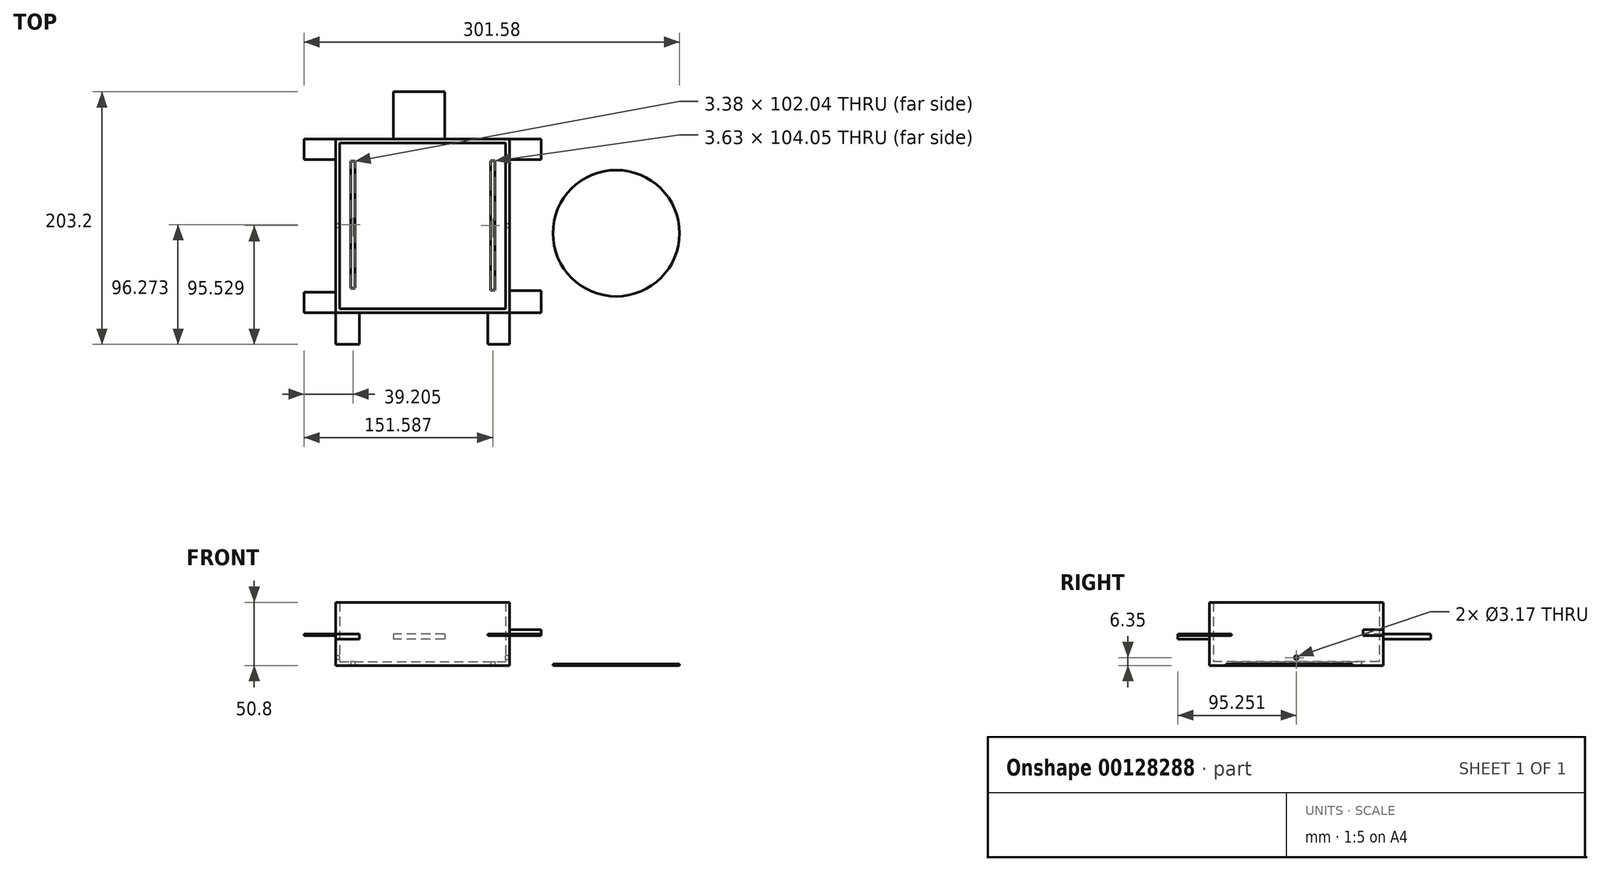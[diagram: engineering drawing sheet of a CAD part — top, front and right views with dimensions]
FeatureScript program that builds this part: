
annotation { "Feature Type Name" : "Feature", "Feature Type Description" : "" }
export const myFeature = defineFeature(function(context is Context, id is Id, definition is map)
    precondition{}
    {
        {
            var Q0;
            Q0=qCreatedBy(makeId("Top.planeOp"),FACE);
            var sketch = newSketch(context, id + "F0", { "sketchPlane" : qUnion([Q0])});
            skLineSegment(sketch, "E0.bottom", {"start": v(-92.8, 73.04) * mm, "end": v(46.9, 73.04) * mm});
            skLineSegment(sketch, "E0.top", {"start": v(-92.8, -66.66) * mm, "end": v(46.9, -66.66) * mm});
            skLineSegment(sketch, "E0.left", {"start": v(-92.8, 73.04) * mm, "end": v(-92.8, -66.66) * mm});
            skLineSegment(sketch, "E0.right", {"start": v(46.9, 73.04) * mm, "end": v(46.9, -66.66) * mm});
            skLineSegment(sketch, "E1.bottom", {"start": v(-92.8, 73.04) * mm, "end": v(-89.63, 73.04) * mm});
            skLineSegment(sketch, "E1.top", {"start": v(-92.8, 69.87) * mm, "end": v(-89.63, 69.87) * mm});
            skLineSegment(sketch, "E1.left", {"start": v(-92.8, 73.04) * mm, "end": v(-92.8, 69.87) * mm});
            skLineSegment(sketch, "E1.right", {"start": v(-89.63, 73.04) * mm, "end": v(-89.63, 69.87) * mm});
            skLineSegment(sketch, "E2.bottom", {"start": v(46.9, -66.66) * mm, "end": v(43.72, -66.66) * mm});
            skLineSegment(sketch, "E2.top", {"start": v(46.9, -63.48) * mm, "end": v(43.72, -63.48) * mm});
            skLineSegment(sketch, "E2.left", {"start": v(46.9, -66.66) * mm, "end": v(46.9, -63.48) * mm});
            skLineSegment(sketch, "E2.right", {"start": v(43.72, -66.66) * mm, "end": v(43.72, -63.48) * mm});
            skLineSegment(sketch, "E3.bottom", {"start": v(-89.63, 69.87) * mm, "end": v(43.72, 69.87) * mm});
            skLineSegment(sketch, "E3.top", {"start": v(-89.63, -63.48) * mm, "end": v(43.72, -63.48) * mm});
            skLineSegment(sketch, "E3.left", {"start": v(-89.63, 69.87) * mm, "end": v(-89.63, -63.48) * mm});
            skLineSegment(sketch, "E3.right", {"start": v(43.72, 69.87) * mm, "end": v(43.72, -63.48) * mm});
            skSolve(sketch);
        }
        {
            var Q0;
            Q0=makeQuery(id+"F0.imprint","IMPRINT",FACE,{"disambiguationData":[TD([[makeQuery(id+"F0.imprint","IMPRINT",EDGE,{"derivedFrom":sQuery(id+"F0.wireOp",EDGE,"E3.bottom")}),-1.0]])]});
            var Q1;
            Q1=makeQuery(id+"F0.imprint","IMPRINT",FACE,{"disambiguationData":[TD([[makeQuery(id+"F0.imprint","IMPRINT",EDGE,{"derivedFrom":sQuery(id+"F0.wireOp",EDGE,"E1.bottom")}),-1.0]])]});
            var Q2;
            Q2=makeQuery(id+"F0.imprint","IMPRINT",FACE,{"disambiguationData":[TD([[makeQuery(id+"F0.imprint","IMPRINT",EDGE,{"derivedFrom":sQuery(id+"F0.wireOp",EDGE,"E0.bottom")}),-1.0]])]});
            var Q3;
            Q3=makeQuery(id+"F0.imprint","IMPRINT",FACE,{"disambiguationData":[TD([[makeQuery(id+"F0.imprint","IMPRINT",EDGE,{"derivedFrom":sQuery(id+"F0.wireOp",EDGE,"E0.top")}),1.0]])]});
            var Q4;
            Q4=makeQuery(id+"F0.imprint","IMPRINT",FACE,{"disambiguationData":[TD([[makeQuery(id+"F0.imprint","IMPRINT",EDGE,{"derivedFrom":sQuery(id+"F0.wireOp",EDGE,"E2.bottom")}),-1.0]])]});
            extrude(context, id + "F1", {"entities" : qUnion([Q0, Q1, Q2, Q3, Q4]), "depth" : 3.17 * mm});
        }
        {
            var Q0;
            Q0 = qSketchRegion(id + "F0", true);
            extrude(context, id + "F2", {"entities" : qUnion([Q0]), "operationType" : NewBodyOperationType.ADD, "depth" : 50.8 * mm});
        }
        {
            var Q0;
            {var subQ0=sQuery(id+"F0.wireOp",EDGE,"E1.bottom");var subQ1=sQuery(id+"F0.wireOp",EDGE,"E0.bottom");Q0=makeQuery(id+"F2.boolean.opBoolean","MERGE",FACE,{"derivedFrom":[makeQuery(id+"F1.opExtrude","SWEPT_FACE",FACE,{"disambiguationData":[OSD([subQ1,subQ0])]}),makeQuery(id+"F2.opExtrude","SWEPT_FACE",FACE,{"disambiguationData":[OSD([subQ1,subQ0])]})]});}
            var sketch = newSketch(context, id + "F3", { "sketchPlane" : qUnion([Q0])});
            skPoint(sketch, "E4.firstSnap0", {"position": v(-46.9, 25.4) * mm});
            skLineSegment(sketch, "E4.bottom", {"start": v(5.25, 25.4) * mm, "end": v(46.35, 25.4) * mm});
            skLineSegment(sketch, "E4.top", {"start": v(5.25, 21.03) * mm, "end": v(46.35, 21.03) * mm});
            skLineSegment(sketch, "E4.left", {"start": v(5.25, 25.4) * mm, "end": v(5.25, 21.03) * mm});
            skLineSegment(sketch, "E4.right", {"start": v(46.35, 25.4) * mm, "end": v(46.35, 21.03) * mm});
            skSolve(sketch);
        }
        {
            var Q0;
            Q0=makeQuery(id+"F3.imprint","IMPRINT",FACE,{"disambiguationData":[TD([[makeQuery(id+"F3.imprint","IMPRINT",EDGE,{"derivedFrom":sQuery(id+"F3.wireOp",EDGE,"E4.bottom")}),-1.0]])]});
            extrude(context, id + "F4", {"entities" : qUnion([Q0]), "operationType" : NewBodyOperationType.ADD, "depth" : 38.1 * mm});
        }
        {
            var Q0;
            {var subQ0=sQuery(id+"F0.wireOp",EDGE,"E1.left");var subQ1=sQuery(id+"F0.wireOp",EDGE,"E0.left");Q0=makeQuery(id+"F2.boolean.opBoolean","MERGE",FACE,{"derivedFrom":[makeQuery(id+"F1.opExtrude","SWEPT_FACE",FACE,{"disambiguationData":[OSD([subQ1,subQ0])]}),makeQuery(id+"F2.opExtrude","SWEPT_FACE",FACE,{"disambiguationData":[OSD([subQ1,subQ0])]})]});}
            var sketch = newSketch(context, id + "F5", { "sketchPlane" : qUnion([Q0])});
            skLineSegment(sketch, "E5.bottom", {"start": v(-73.04, 25.4) * mm, "end": v(-56.47, 25.4) * mm});
            skLineSegment(sketch, "E5.top", {"start": v(-73.04, 24.18) * mm, "end": v(-56.47, 24.18) * mm});
            skLineSegment(sketch, "E5.left", {"start": v(-73.04, 25.4) * mm, "end": v(-73.04, 24.18) * mm});
            skLineSegment(sketch, "E5.right", {"start": v(-56.47, 25.4) * mm, "end": v(-56.47, 24.18) * mm});
            skPoint(sketch, "E6.oppositeSnap0", {"position": v(66.66, 25.4) * mm});
            skLineSegment(sketch, "E6.bottom", {"start": v(66.66, 24.18) * mm, "end": v(50.17, 24.18) * mm});
            skLineSegment(sketch, "E6.top", {"start": v(66.66, 25.4) * mm, "end": v(50.17, 25.4) * mm});
            skLineSegment(sketch, "E6.left", {"start": v(66.66, 24.18) * mm, "end": v(66.66, 25.4) * mm});
            skLineSegment(sketch, "E6.right", {"start": v(50.17, 24.18) * mm, "end": v(50.17, 25.4) * mm});
            skSolve(sketch);
        }
        {
            var Q0;
            Q0=makeQuery(id+"F5.imprint","IMPRINT",FACE,{"disambiguationData":[TD([[makeQuery(id+"F5.imprint","IMPRINT",EDGE,{"derivedFrom":sQuery(id+"F5.wireOp",EDGE,"E5.bottom")}),-1.0]])]});
            var Q1;
            Q1=makeQuery(id+"F5.imprint","IMPRINT",FACE,{"disambiguationData":[TD([[makeQuery(id+"F5.imprint","IMPRINT",EDGE,{"derivedFrom":sQuery(id+"F5.wireOp",EDGE,"E6.bottom")}),-1.0]])]});
            extrude(context, id + "F6", {"entities" : qUnion([Q0, Q1]), "operationType" : NewBodyOperationType.ADD, "depth" : 25.4 * mm});
        }
        {
            var Q0;
            {var subQ0=sQuery(id+"F0.wireOp",EDGE,"E2.left");var subQ1=sQuery(id+"F0.wireOp",EDGE,"E0.right");Q0=makeQuery(id+"F2.boolean.opBoolean","MERGE",FACE,{"derivedFrom":[makeQuery(id+"F1.opExtrude","SWEPT_FACE",FACE,{"disambiguationData":[OSD([subQ1,subQ0])]}),makeQuery(id+"F2.opExtrude","SWEPT_FACE",FACE,{"disambiguationData":[OSD([subQ1,subQ0])]})]});}
            var sketch = newSketch(context, id + "F7", { "sketchPlane" : qUnion([Q0])});
            skLineSegment(sketch, "E7.bottom", {"start": v(73.04, 23.98) * mm, "end": v(56.72, 23.98) * mm});
            skLineSegment(sketch, "E7.top", {"start": v(73.04, 28.65) * mm, "end": v(56.72, 28.65) * mm});
            skLineSegment(sketch, "E7.left", {"start": v(73.04, 23.98) * mm, "end": v(73.04, 28.65) * mm});
            skLineSegment(sketch, "E7.right", {"start": v(56.72, 23.98) * mm, "end": v(56.72, 28.65) * mm});
            skLineSegment(sketch, "E8.bottom", {"start": v(-66.66, 25.4) * mm, "end": v(-48.97, 25.4) * mm});
            skLineSegment(sketch, "E8.top", {"start": v(-66.66, 23.98) * mm, "end": v(-48.97, 23.98) * mm});
            skLineSegment(sketch, "E8.left", {"start": v(-66.66, 25.4) * mm, "end": v(-66.66, 23.98) * mm});
            skLineSegment(sketch, "E8.right", {"start": v(-48.97, 25.4) * mm, "end": v(-48.97, 23.98) * mm});
            skSolve(sketch);
        }
        {
            var Q0;
            Q0=makeQuery(id+"F7.imprint","IMPRINT",FACE,{"disambiguationData":[TD([[makeQuery(id+"F7.imprint","IMPRINT",EDGE,{"derivedFrom":sQuery(id+"F7.wireOp",EDGE,"E8.bottom")}),-1.0]])]});
            var Q1;
            Q1=makeQuery(id+"F7.imprint","IMPRINT",FACE,{"disambiguationData":[TD([[makeQuery(id+"F7.imprint","IMPRINT",EDGE,{"derivedFrom":sQuery(id+"F7.wireOp",EDGE,"E7.bottom")}),-1.0]])]});
            extrude(context, id + "F8", {"entities" : qUnion([Q0, Q1]), "operationType" : NewBodyOperationType.ADD, "depth" : 25.4 * mm});
        }
        {
            var Q0;
            {var subQ0=sQuery(id+"F0.wireOp",EDGE,"E2.bottom");var subQ1=sQuery(id+"F0.wireOp",EDGE,"E0.top");Q0=makeQuery(id+"F8.boolean.opBoolean","MERGE",FACE,{"derivedFrom":[makeQuery(id+"F6.boolean.opBoolean","MERGE",FACE,{"derivedFrom":[makeQuery(id+"F2.boolean.opBoolean","MERGE",FACE,{"derivedFrom":[makeQuery(id+"F1.opExtrude","SWEPT_FACE",FACE,{"disambiguationData":[OSD([subQ1,subQ0])]}),makeQuery(id+"F2.opExtrude","SWEPT_FACE",FACE,{"disambiguationData":[OSD([subQ1,subQ0])]})]}),makeQuery(id+"F6.opExtrude","SWEPT_FACE",FACE,{"disambiguationData":[OSD([sQuery(id+"F5.wireOp",EDGE,"E6.left")])]})]}),makeQuery(id+"F8.opExtrude","SWEPT_FACE",FACE,{"disambiguationData":[OSD([sQuery(id+"F7.wireOp",EDGE,"E8.left")])]})]});}
            var sketch = newSketch(context, id + "F9", { "sketchPlane" : qUnion([Q0])});
            skLineSegment(sketch, "E9.bottom", {"start": v(-92.8, 25.4) * mm, "end": v(-73.77, 25.4) * mm});
            skLineSegment(sketch, "E9.top", {"start": v(-92.8, 21.13) * mm, "end": v(-73.77, 21.13) * mm});
            skLineSegment(sketch, "E9.left", {"start": v(-92.8, 25.4) * mm, "end": v(-92.8, 21.13) * mm});
            skLineSegment(sketch, "E9.right", {"start": v(-73.77, 25.4) * mm, "end": v(-73.77, 21.13) * mm});
            skLineSegment(sketch, "E10.bottom", {"start": v(46.9, 25.4) * mm, "end": v(29.3, 25.4) * mm});
            skLineSegment(sketch, "E10.top", {"start": v(46.9, 23.98) * mm, "end": v(29.3, 23.98) * mm});
            skLineSegment(sketch, "E10.left", {"start": v(46.9, 25.4) * mm, "end": v(46.9, 23.98) * mm});
            skLineSegment(sketch, "E10.right", {"start": v(29.3, 25.4) * mm, "end": v(29.3, 23.98) * mm});
            skSolve(sketch);
        }
        {
            var Q0;
            Q0=makeQuery(id+"F9.imprint","IMPRINT",FACE,{"disambiguationData":[TD([[makeQuery(id+"F9.imprint","IMPRINT",EDGE,{"derivedFrom":sQuery(id+"F9.wireOp",EDGE,"E9.bottom")}),-1.0]])]});
            var Q1;
            Q1=makeQuery(id+"F9.imprint","IMPRINT",FACE,{"disambiguationData":[TD([[makeQuery(id+"F9.imprint","IMPRINT",EDGE,{"derivedFrom":sQuery(id+"F9.wireOp",EDGE,"E10.bottom")}),1.0]])]});
            extrude(context, id + "F10", {"entities" : qUnion([Q0, Q1]), "operationType" : NewBodyOperationType.ADD, "depth" : 25.4 * mm});
        }
        {
            var Q0;
            {var subQ0=sQuery(id+"F0.wireOp",EDGE,"E1.left");var subQ1=sQuery(id+"F0.wireOp",EDGE,"E0.left");Q0=makeQuery(id+"F2.boolean.opBoolean","MERGE",FACE,{"derivedFrom":[makeQuery(id+"F1.opExtrude","SWEPT_FACE",FACE,{"disambiguationData":[OSD([subQ1,subQ0])]}),makeQuery(id+"F2.opExtrude","SWEPT_FACE",FACE,{"disambiguationData":[OSD([subQ1,subQ0])]})]});}
            var sketch = newSketch(context, id + "F11", { "sketchPlane" : qUnion([Q0])});
            skCircle(sketch, "E11", {"center": v(-3.2, 6.35) * mm, "radius": 1.59 * mm});
            skSolve(sketch);
        }
        {
            var Q0;
            Q0=sQuery(id+"F11.wireOp",VERTEX,"E11.center");
            var Q1;
            Q1=makeQuery(id+"F1.opExtrude","SWEPT_BODY",BODY,{"disambiguationData":[OSD([sQuery(id+"F0.wireOp",EDGE,"E0.bottom"),sQuery(id+"F0.wireOp",EDGE,"E0.top"),sQuery(id+"F0.wireOp",EDGE,"E0.left"),sQuery(id+"F0.wireOp",EDGE,"E0.right"),sQuery(id+"F0.wireOp",EDGE,"E1.bottom"),sQuery(id+"F0.wireOp",EDGE,"E1.left"),sQuery(id+"F0.wireOp",EDGE,"E2.bottom"),sQuery(id+"F0.wireOp",EDGE,"E2.left")])]});
            hole(context, id + "F12", {"style" : HoleStyle.SIMPLE, "endStyle" : HoleEndStyle.THROUGH, "holeDiameter" : 3.17 * mm, "locations" : qUnion([Q0]), "scope" : qUnion([Q1]), "isTappedThrough" : true});
        }
        {
            var Q0;
            Q0=makeQuery(id+"F0.imprint","IMPRINT",FACE,{"disambiguationData":[TD([[makeQuery(id+"F0.imprint","IMPRINT",EDGE,{"derivedFrom":sQuery(id+"F0.wireOp",EDGE,"E3.bottom")}),-1.0]])]});
            var sketch = newSketch(context, id + "F13", { "sketchPlane" : qUnion([Q0])});
            skLineSegment(sketch, "E12.bottom", {"start": v(35.2, 55.5) * mm, "end": v(31.56, 55.5) * mm});
            skLineSegment(sketch, "E12.top", {"start": v(35.2, -48.56) * mm, "end": v(31.56, -48.56) * mm});
            skLineSegment(sketch, "E12.left", {"start": v(35.2, 55.5) * mm, "end": v(35.2, -48.56) * mm});
            skLineSegment(sketch, "E12.right", {"start": v(31.56, 55.5) * mm, "end": v(31.56, -48.56) * mm});
            skLineSegment(sketch, "E13.bottom", {"start": v(-80.7, 55.24) * mm, "end": v(-77.32, 55.24) * mm});
            skLineSegment(sketch, "E13.top", {"start": v(-80.7, -46.8) * mm, "end": v(-77.32, -46.8) * mm});
            skLineSegment(sketch, "E13.left", {"start": v(-80.7, 55.24) * mm, "end": v(-80.7, -46.8) * mm});
            skLineSegment(sketch, "E13.right", {"start": v(-77.32, 55.24) * mm, "end": v(-77.32, -46.8) * mm});
            skSolve(sketch);
        }
        {
            var Q0;
            Q0=makeQuery(id+"F13.imprint","IMPRINT",FACE,{"disambiguationData":[TD([[makeQuery(id+"F13.imprint","IMPRINT",EDGE,{"derivedFrom":sQuery(id+"F13.wireOp",EDGE,"E13.bottom")}),-1.0]])]});
            var Q1;
            Q1=makeQuery(id+"F13.imprint","IMPRINT",FACE,{"disambiguationData":[TD([[makeQuery(id+"F13.imprint","IMPRINT",EDGE,{"derivedFrom":sQuery(id+"F13.wireOp",EDGE,"E12.bottom")}),1.0]])]});
            extrude(context, id + "F14", {"entities" : qUnion([Q0, Q1]), "operationType" : NewBodyOperationType.REMOVE, "depth" : 25.4 * mm});
        }
        {
            var Q0;
            Q0=qCreatedBy(makeId("Top.planeOp"),FACE);
            var sketch = newSketch(context, id + "F15", { "sketchPlane" : qUnion([Q0])});
            skCircle(sketch, "E14", {"center": v(132.57, -2.64) * mm, "radius": 50.8 * mm});
            skSolve(sketch);
        }
        {
            var Q0;
            Q0=makeQuery(id+"F15.imprint","IMPRINT",FACE,{"disambiguationData":[TD([[makeQuery(id+"F15.imprint","IMPRINT",EDGE,{"derivedFrom":sQuery(id+"F15.wireOp",EDGE,"E14")}),1.0]])]});
            extrude(context, id + "F16", {"entities" : qUnion([Q0]), "depth" : 1.27 * mm});
        }
    });
